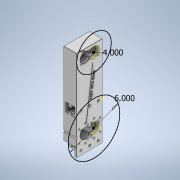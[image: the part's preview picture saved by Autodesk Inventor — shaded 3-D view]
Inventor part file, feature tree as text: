
AUTODESK INVENTOR PART (.ipt)
format: ipt  version: 2020 (Build 240168000, 168)  size: 822,784 bytes
history: native  units: in
note: dims shown in document units (in); Inventor stores cm internally (conversion verified against a paired STEP export)
features: reference x24, extrude x10, sketch x10, other x4, chamfer x1, fillet x1
ambient origin geometry x8: Origin, YZ Plane, XZ Plane, XY Plane, X Axis, Y Axis, Z Axis, Center Point
bodies: Solid1 (feature_tree)
feature tree (50):
  extrude  "Extrusion1"  Depth=5.0in
  extrude  "Extrusion2"  Depth=3.0in TaperAngle=0.0deg
  extrude  "Extrusion4"  TaperAngle=0.0deg  [1 undecoded]
  extrude  "Extrusion5"  Depth=1.126in
  extrude  "Extrusion6"  Depth=1.226in
  extrude  "Extrusion7"  Depth=1.126in
  extrude  "Extrusion8"  Depth=1.226in
  chamfer  "Chamfer3"  Distance=0.064in
  extrude  "Extrusion9"  Depth=0.165in
  fillet  "Fillet1"  [1 undecoded]
  sketch  "Sketch13"  dims[d50=1.4291in d51=0.165in d52=0.0in d53=0.0in]
  extrude  "Extrusion11"  Depth=1.0in
  extrude  "Extrusion12"  Depth=3.1496in TaperAngle=360.0deg
  reference  "Reference1"
  reference  "Reference2"
  reference  "Reference3"
  reference  "Reference4"
  reference  "Reference5"
  reference  "Reference6"
  reference  "Reference7"
  reference  "Reference8"
  reference  "Reference9"
  reference  "Reference10"
  reference  "Reference11"
  reference  "Reference12"
  reference  "Reference13"
  reference  "Reference14"
  reference  "Reference15"
  reference  "Reference16"
  reference  "Reference17"
  reference  "Reference18"
  reference  "Reference19"
  reference  "Reference20"
  reference  "Reference21"
  reference  "Reference22"
  reference  "Reference23"
  reference  "Reference24"
  sketch  "Sketch2"  dims[d0=1.5in d1=5.0in]
  sketch  "Sketch4"  dims[d2=0.2461in d3=3.0in d4=0.0in]
  sketch  "Sketch5"  dims[d7=0.2656in d24=0.0in d25=0.0in]
  sketch  "Sketch6"  dims[d31=1.023in d32=1.126in]
  sketch  "Sketch7"  dims[d33=0.314in d34=0.0in d35=1.226in]
  sketch  "Sketch8"  dims[d36=0.064in d37=0.0in d41=1.126in]
  sketch  "Sketch9"  dims[d42=0.314in d43=0.0in d44=1.226in d45=0.064in d46=0.0in]
  sketch  "Sketch14"  dims[d54=0.025in d55=0.125in d56=45.0deg d57=1.0in]
  sketch  "Sketch15"  dims[d58=0.196in d59=3.1496in d61=360.0deg d63=0.0in d64=0.0in d76=0.25in d77=5.5in d78=0.5in d79=0.5in d80=0.7874in d82=4.0in d83=1.1811in d85=1.0in d89=1.0in d90=2.0in d93=7.6781in d94=1.0in d95=1.0in d96=3.1496in d98=360.0deg d100=0.125in d101=4.0in d102=6.0in d103=0.05in d104=1.0in d105=1.0in d106=0.05in d107=0.0in d108=0.1in d109=0.05in d110=0.0in]
  other  "<userpath>\Documents\FRC\2020\ShooterPrototype.iam"
  other  "ShooterPrototype.iam"
  other  "9inSpacer:1"
  other  "1003-48-CL:4"
note: 2 required parameter values undecoded (feature->parameter linkage not recoverable at this tier; creation-order binding heuristic only, values carry confidence <= 0.55)
